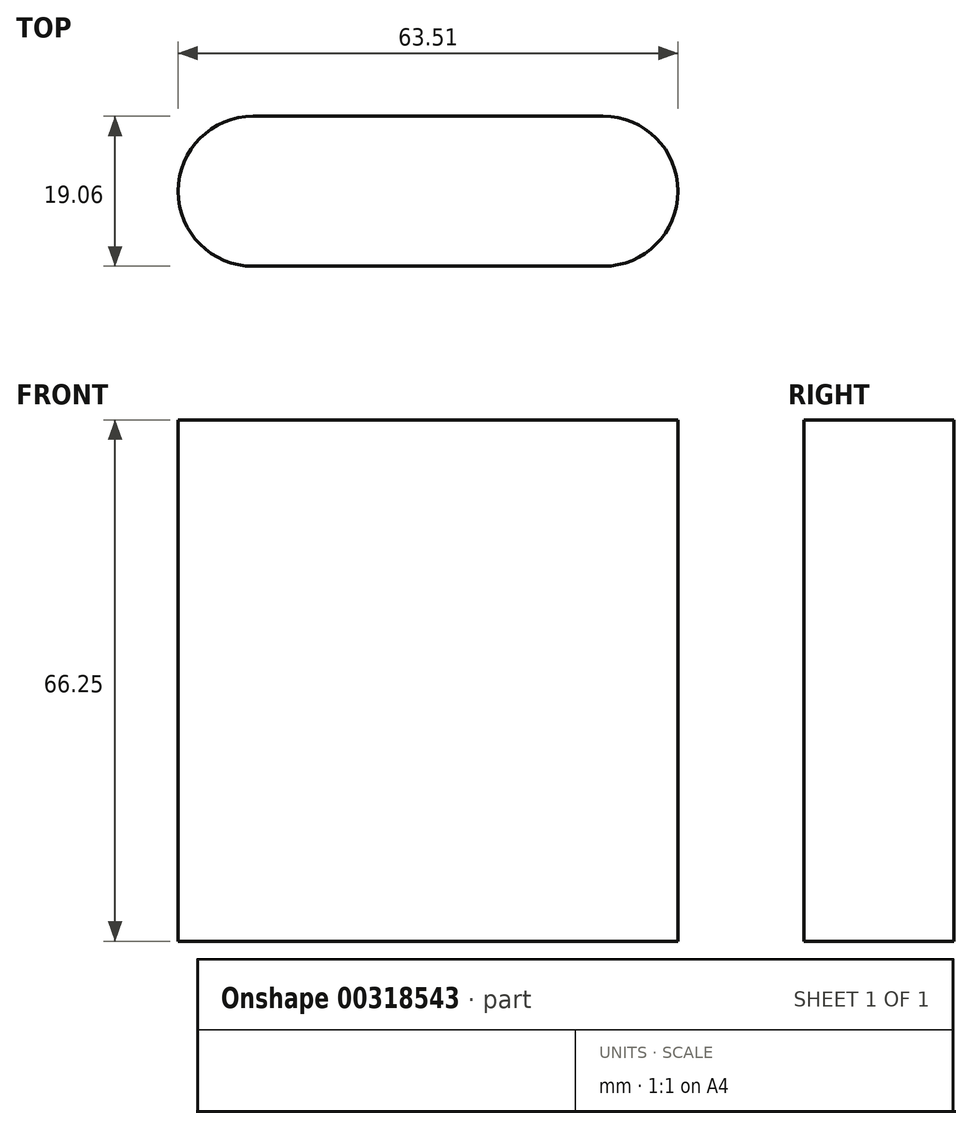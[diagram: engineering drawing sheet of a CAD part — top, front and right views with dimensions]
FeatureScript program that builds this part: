
annotation { "Feature Type Name" : "Feature", "Feature Type Description" : "" }
export const myFeature = defineFeature(function(context is Context, id is Id, definition is map)
    precondition{}
    {
        {
            var Q0;
            Q0=qCreatedBy(makeId("Top.planeOp"),FACE);
            var sketch = newSketch(context, id + "F0", { "sketchPlane" : qUnion([Q0])});
            skCircle(sketch, "E0", {"center": v(0, 0) * mm, "radius": 9.53 * mm});
            skCircle(sketch, "E1", {"center": v(44.45, 0) * mm, "radius": 9.53 * mm});
            skLineSegment(sketch, "E2", {"start": v(0, 9.53) * mm, "end": v(44.45, 9.53) * mm});
            skLineSegment(sketch, "E3", {"start": v(0, -9.53) * mm, "end": v(44.45, -9.53) * mm});
            skSolve(sketch);
        }
        {
            var Q0;
            Q0 = qSketchRegion(id + "F0", true);
            extrude(context, id + "F1", {"entities" : qUnion([Q0]), "depth" : 25.4 * mm});
        }
        {
            var Q0;
            Q0=makeQuery(id+"F1.opExtrude","CAP_FACE",FACE,{"disambiguationData":[OSD([sQuery(id+"F0.wireOp",EDGE,"E0"),sQuery(id+"F0.wireOp",EDGE,"E1"),sQuery(id+"F0.wireOp",EDGE,"E2"),sQuery(id+"F0.wireOp",EDGE,"E3")])],"isStart":false});
            var sketch = newSketch(context, id + "F2", { "sketchPlane" : qUnion([Q0])});
            skCircle(sketch, "E4", {"center": v(0, 0) * mm, "radius": 7.15 * mm});
            skCircle(sketch, "E5", {"center": v(44.45, 0) * mm, "radius": 7.42 * mm});
            skSolve(sketch);
        }
        {
            var Q0;
            Q0=sQuery(id+"F2.wireOp",EDGE,"E4");
            var Q1;
            Q1=sQuery(id+"F2.wireOp",EDGE,"E5");
            extrude(context, id + "F3", {"bodyType" : ToolBodyType.SURFACE, "operationType" : NewBodyOperationType.REMOVE, "surfaceEntities" : qUnion([Q0, Q1]), "endBound" : BoundingType.THROUGH_ALL, "oppositeDirection" : true, "depth" : 25.4 * mm});
        }
        {
            var Q0;
            Q0=makeQuery(id+"F1.opExtrude","CAP_FACE",FACE,{"disambiguationData":[OSD([sQuery(id+"F0.wireOp",EDGE,"E0"),sQuery(id+"F0.wireOp",EDGE,"E1"),sQuery(id+"F0.wireOp",EDGE,"E2"),sQuery(id+"F0.wireOp",EDGE,"E3")])],"isStart":true});
            extrude(context, id + "F4", {"entities" : qUnion([Q0]), "operationType" : NewBodyOperationType.ADD, "depth" : 40.85 * mm});
        }
    });
